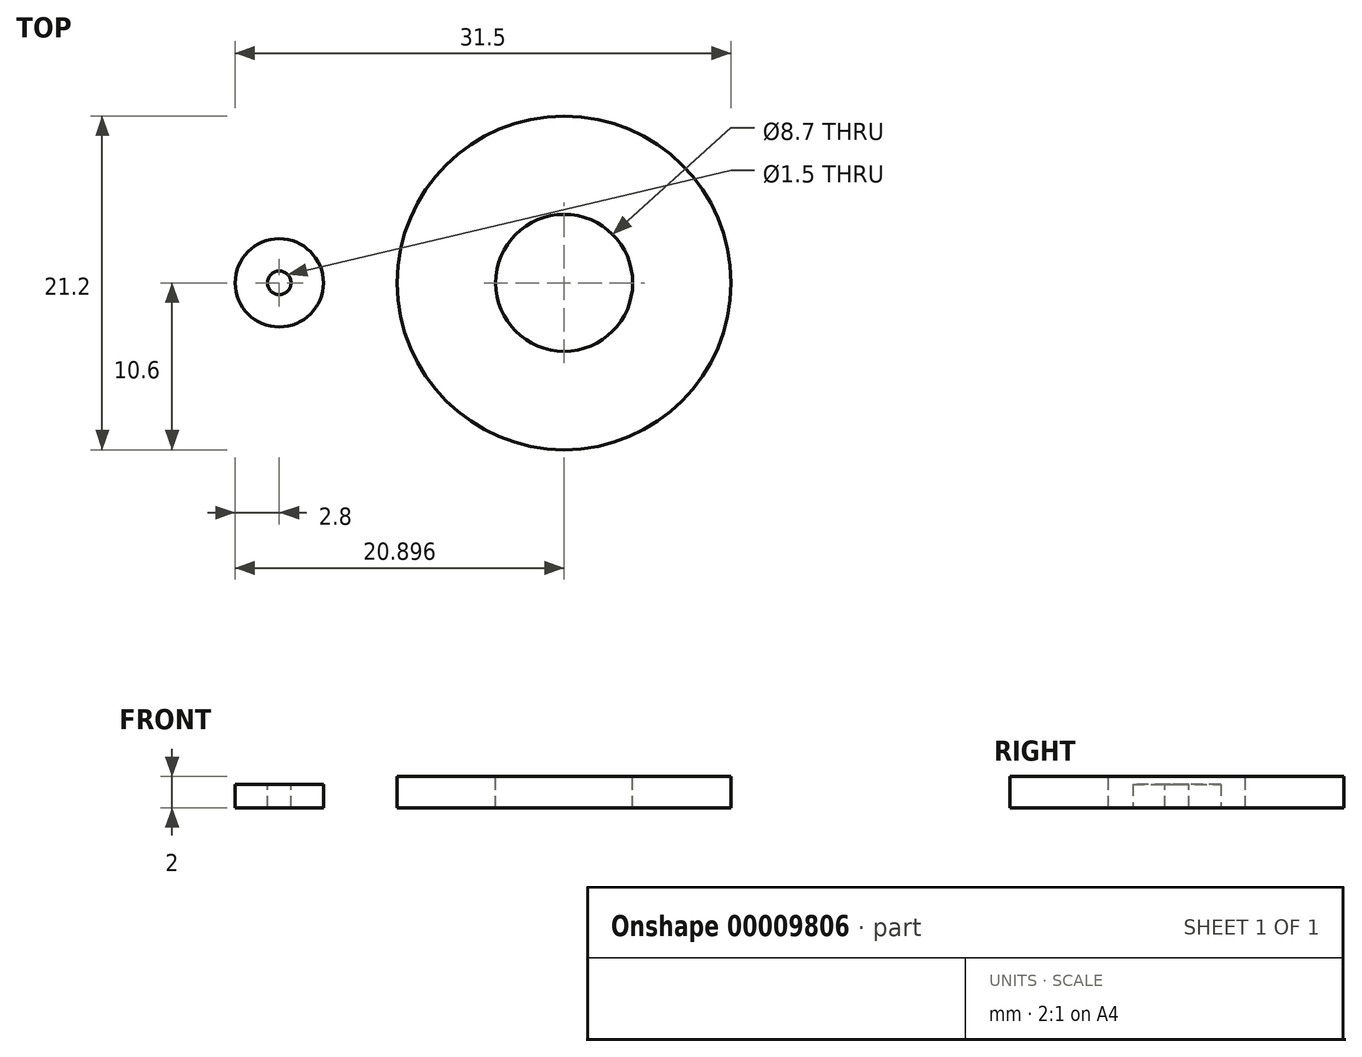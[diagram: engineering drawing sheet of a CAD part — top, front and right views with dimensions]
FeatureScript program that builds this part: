
annotation { "Feature Type Name" : "Feature", "Feature Type Description" : "" }
export const myFeature = defineFeature(function(context is Context, id is Id, definition is map)
    precondition{}
    {
        {
            var Q0;
            Q0=qCreatedBy(makeId("Top.planeOp"),FACE);
            var sketch = newSketch(context, id + "F0", { "sketchPlane" : qUnion([Q0])});
            skCircle(sketch, "E0", {"center": v(0, 0) * mm, "radius": 2.8 * mm});
            skSolve(sketch);
        }
        {
            var Q0;
            Q0=makeQuery(id+"F0.imprint","IMPRINT",FACE,{"disambiguationData":[TD([[makeQuery(id+"F0.imprint","IMPRINT",EDGE,{"derivedFrom":sQuery(id+"F0.wireOp",EDGE,"E0")}),1.0]])]});
            extrude(context, id + "F1", {"entities" : qUnion([Q0]), "depth" : 1.5 * mm});
        }
        {
            var Q0;
            Q0=makeQuery(id+"F1.opExtrude","CAP_FACE",FACE,{"disambiguationData":[OSD([sQuery(id+"F0.wireOp",EDGE,"E0")])],"isStart":false});
            var sketch = newSketch(context, id + "F2", { "sketchPlane" : qUnion([Q0])});
            skCircle(sketch, "E1", {"center": v(0, 0) * mm, "radius": 0.75 * mm});
            skSolve(sketch);
        }
        {
            var Q0;
            Q0=makeQuery(id+"F2.imprint","IMPRINT",FACE,{"disambiguationData":[TD([[makeQuery(id+"F2.imprint","IMPRINT",EDGE,{"derivedFrom":sQuery(id+"F2.wireOp",EDGE,"E1")}),1.0]])]});
            extrude(context, id + "F3", {"entities" : qUnion([Q0]), "operationType" : NewBodyOperationType.REMOVE, "oppositeDirection" : true, "depth" : 25 * mm});
        }
        {
            var Q0;
            Q0=qCreatedBy(makeId("Top.planeOp"),FACE);
            var sketch = newSketch(context, id + "F4", { "sketchPlane" : qUnion([Q0])});
            skCircle(sketch, "E2", {"center": v(18.1, 0) * mm, "radius": 10.6 * mm});
            skSolve(sketch);
        }
        {
            var Q0;
            Q0 = qSketchRegion(id + "F4", true);
            extrude(context, id + "F5", {"entities" : qUnion([Q0]), "depth" : 2 * mm});
        }
        {
            var Q0;
            Q0=makeQuery(id+"F5.opExtrude","CAP_FACE",FACE,{"disambiguationData":[OSD([sQuery(id+"F4.wireOp",EDGE,"E2")])],"isStart":false});
            var sketch = newSketch(context, id + "F6", { "sketchPlane" : qUnion([Q0])});
            skCircle(sketch, "E3", {"center": v(18.1, 0) * mm, "radius": 4.35 * mm});
            skSolve(sketch);
        }
        {
            var Q0;
            Q0=makeQuery(id+"F6.imprint","IMPRINT",FACE,{"disambiguationData":[TD([[makeQuery(id+"F6.imprint","IMPRINT",EDGE,{"derivedFrom":sQuery(id+"F6.wireOp",EDGE,"E3")}),1.0]])]});
            extrude(context, id + "F7", {"entities" : qUnion([Q0]), "operationType" : NewBodyOperationType.REMOVE, "oppositeDirection" : true, "depth" : 25 * mm});
        }
    });
